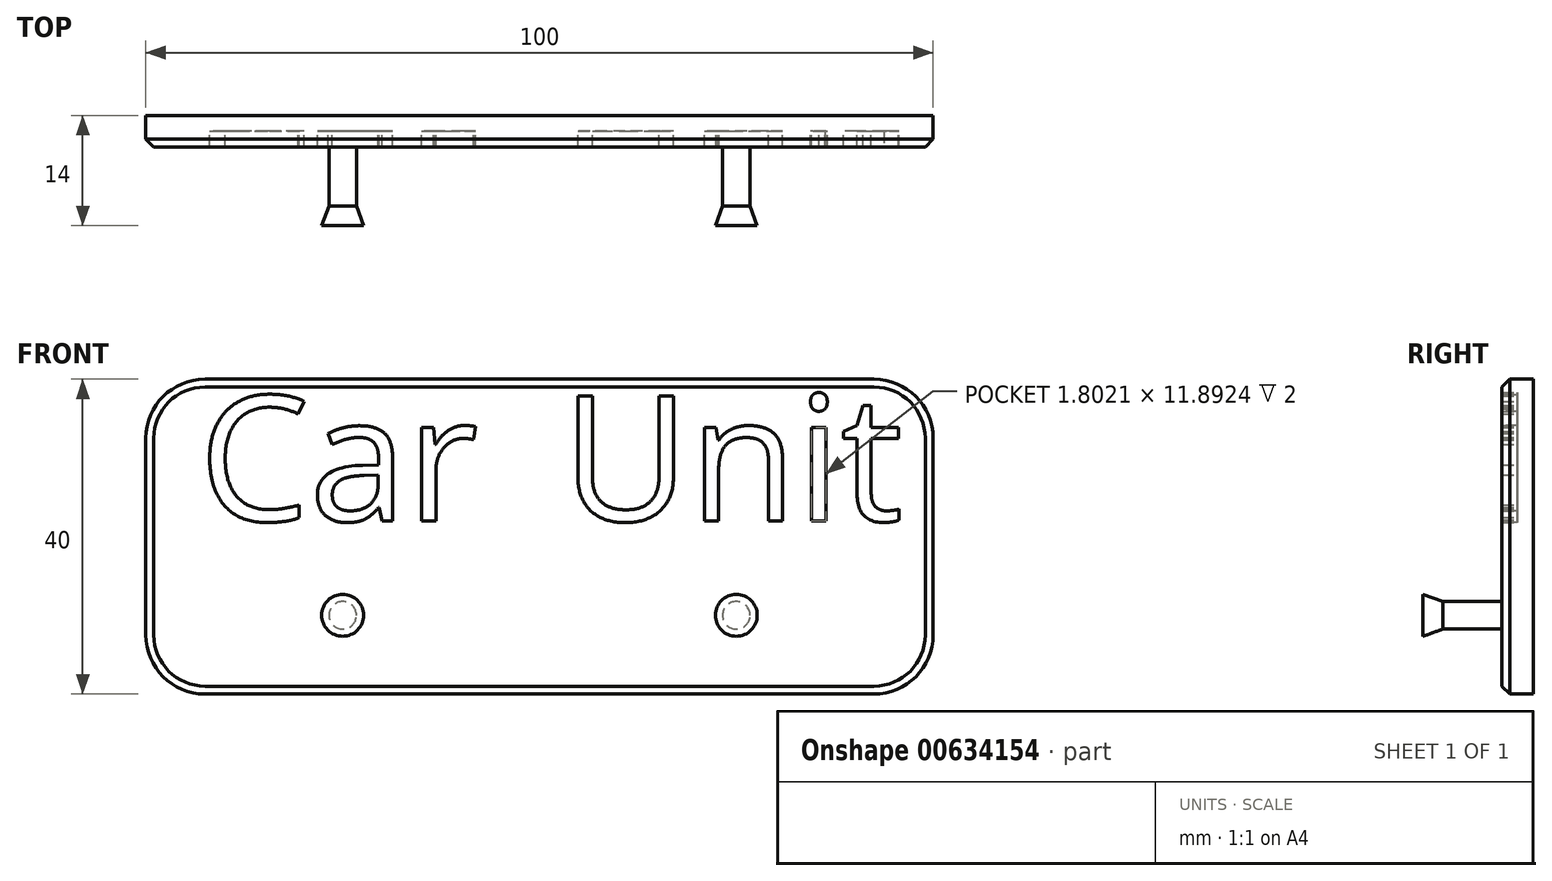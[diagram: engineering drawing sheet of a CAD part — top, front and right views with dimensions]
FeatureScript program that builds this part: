
annotation { "Feature Type Name" : "Feature", "Feature Type Description" : "" }
export const myFeature = defineFeature(function(context is Context, id is Id, definition is map)
    precondition{}
    {
        {
            var Q0;
            Q0=qCreatedBy(makeId("Front.planeOp"),FACE);
            var sketch = newSketch(context, id + "F0", { "sketchPlane" : qUnion([Q0])});
            skLineSegment(sketch, "E0.bottom", {"start": v(-50, 20) * mm, "end": v(50, 20) * mm});
            skLineSegment(sketch, "E0.top", {"start": v(-50, -20) * mm, "end": v(50, -20) * mm});
            skLineSegment(sketch, "E0.left", {"start": v(-50, 20) * mm, "end": v(-50, -20) * mm});
            skLineSegment(sketch, "E0.right", {"start": v(50, 20) * mm, "end": v(50, -20) * mm});
            skText(sketch, "E1", { "text": "Car\n", "fontName": "OpenSans-Regular.ttf"});
            skText(sketch, "E2", { "text": "Unit\n", "fontName": "OpenSans-Regular.ttf"});
            const initialGuessF0  = {"E1": [-0.04325, 0.002, 1, 0, 0.016], "E2": [0.00286, 0.002, 1, 0, 0.016]};
            skSetInitialGuess(sketch, initialGuessF0);
            skSolve(sketch);
        }
        {
            var Q0;
            Q0=makeQuery(id+"F0.imprint","IMPRINT",FACE,{"disambiguationData":[TD([[makeQuery(id+"F0.imprint","IMPRINT",EDGE,{"derivedFrom":sQuery(id+"F0.wireOp",EDGE,"E2.sketch_text.stroke-31")}),-1.0]])]});
            var Q1;
            Q1=makeQuery(id+"F0.imprint","IMPRINT",FACE,{"disambiguationData":[TD([[makeQuery(id+"F0.imprint","IMPRINT",EDGE,{"derivedFrom":sQuery(id+"F0.wireOp",EDGE,"E2.sketch_text.stroke-35")}),-1.0]])]});
            var Q2;
            Q2=makeQuery(id+"F0.imprint","IMPRINT",FACE,{"disambiguationData":[TD([[makeQuery(id+"F0.imprint","IMPRINT",EDGE,{"derivedFrom":sQuery(id+"F0.wireOp",EDGE,"E0.bottom")}),-1.0]])]});
            var Q3;
            Q3=makeQuery(id+"F0.imprint","IMPRINT",FACE,{"disambiguationData":[TD([[makeQuery(id+"F0.imprint","IMPRINT",EDGE,{"derivedFrom":sQuery(id+"F0.wireOp",EDGE,"E2.sketch_text.stroke-43")}),-1.0]])]});
            var Q4;
            Q4=makeQuery(id+"F0.imprint","IMPRINT",FACE,{"disambiguationData":[TD([[makeQuery(id+"F0.imprint","IMPRINT",EDGE,{"derivedFrom":sQuery(id+"F0.wireOp",EDGE,"E2.sketch_text.stroke-14")}),-1.0]])]});
            var Q5;
            Q5=makeQuery(id+"F0.imprint","IMPRINT",FACE,{"disambiguationData":[TD([[makeQuery(id+"F0.imprint","IMPRINT",EDGE,{"derivedFrom":sQuery(id+"F0.wireOp",EDGE,"E2.sketch_text.stroke-0")}),-1.0]])]});
            var Q6;
            Q6=makeQuery(id+"F0.imprint","IMPRINT",FACE,{"disambiguationData":[TD([[makeQuery(id+"F0.imprint","IMPRINT",EDGE,{"derivedFrom":sQuery(id+"F0.wireOp",EDGE,"E1.sketch_text.stroke-42")}),-1.0]])]});
            var Q7;
            Q7=makeQuery(id+"F0.imprint","IMPRINT",FACE,{"disambiguationData":[TD([[makeQuery(id+"F0.imprint","IMPRINT",EDGE,{"derivedFrom":sQuery(id+"F0.wireOp",EDGE,"E1.sketch_text.stroke-34")}),1.0]])]});
            var Q8;
            Q8=makeQuery(id+"F0.imprint","IMPRINT",FACE,{"disambiguationData":[TD([[makeQuery(id+"F0.imprint","IMPRINT",EDGE,{"derivedFrom":sQuery(id+"F0.wireOp",EDGE,"E1.sketch_text.stroke-15")}),-1.0]])]});
            var Q9;
            Q9=makeQuery(id+"F0.imprint","IMPRINT",FACE,{"disambiguationData":[TD([[makeQuery(id+"F0.imprint","IMPRINT",EDGE,{"derivedFrom":sQuery(id+"F0.wireOp",EDGE,"E1.sketch_text.stroke-0")}),-1.0]])]});
            extrude(context, id + "F1", {"entities" : qUnion([Q0, Q1, Q2, Q3, Q4, Q5, Q6, Q7, Q8, Q9]), "oppositeDirection" : true, "depth" : 2 * mm, "offsetDistance" : 25 * mm});
        }
        {
            var Q0;
            Q0=makeQuery(id+"F0.imprint","IMPRINT",FACE,{"disambiguationData":[TD([[makeQuery(id+"F0.imprint","IMPRINT",EDGE,{"derivedFrom":sQuery(id+"F0.wireOp",EDGE,"E0.bottom")}),-1.0]])]});
            var Q1;
            Q1=makeQuery(id+"F0.imprint","IMPRINT",FACE,{"disambiguationData":[TD([[makeQuery(id+"F0.imprint","IMPRINT",EDGE,{"derivedFrom":sQuery(id+"F0.wireOp",EDGE,"E1.sketch_text.stroke-34")}),1.0]])]});
            extrude(context, id + "F2", {"entities" : qUnion([Q0, Q1]), "operationType" : NewBodyOperationType.ADD, "depth" : 2 * mm, "offsetDistance" : 25 * mm});
        }
        {
            var Q0;
            Q0=makeQuery(id+"F2.opExtrude","CAP_FACE",FACE,{"disambiguationData":[OSD([sQuery(id+"F0.wireOp",EDGE,"E0.bottom"),sQuery(id+"F0.wireOp",EDGE,"E0.top"),sQuery(id+"F0.wireOp",EDGE,"E0.left"),sQuery(id+"F0.wireOp",EDGE,"E0.right"),sQuery(id+"F0.wireOp",EDGE,"E1.sketch_text.stroke-0"),sQuery(id+"F0.wireOp",EDGE,"E1.sketch_text.stroke-1"),sQuery(id+"F0.wireOp",EDGE,"E1.sketch_text.stroke-2"),sQuery(id+"F0.wireOp",EDGE,"E1.sketch_text.stroke-3"),sQuery(id+"F0.wireOp",EDGE,"E1.sketch_text.stroke-4"),sQuery(id+"F0.wireOp",EDGE,"E1.sketch_text.stroke-5"),sQuery(id+"F0.wireOp",EDGE,"E1.sketch_text.stroke-6"),sQuery(id+"F0.wireOp",EDGE,"E1.sketch_text.stroke-7"),sQuery(id+"F0.wireOp",EDGE,"E1.sketch_text.stroke-8"),sQuery(id+"F0.wireOp",EDGE,"E1.sketch_text.stroke-9"),sQuery(id+"F0.wireOp",EDGE,"E1.sketch_text.stroke-10"),sQuery(id+"F0.wireOp",EDGE,"E1.sketch_text.stroke-11"),sQuery(id+"F0.wireOp",EDGE,"E1.sketch_text.stroke-12"),sQuery(id+"F0.wireOp",EDGE,"E1.sketch_text.stroke-13"),sQuery(id+"F0.wireOp",EDGE,"E1.sketch_text.stroke-14"),sQuery(id+"F0.wireOp",EDGE,"E1.sketch_text.stroke-15"),sQuery(id+"F0.wireOp",EDGE,"E1.sketch_text.stroke-16"),sQuery(id+"F0.wireOp",EDGE,"E1.sketch_text.stroke-17"),sQuery(id+"F0.wireOp",EDGE,"E1.sketch_text.stroke-18"),sQuery(id+"F0.wireOp",EDGE,"E1.sketch_text.stroke-19"),sQuery(id+"F0.wireOp",EDGE,"E1.sketch_text.stroke-20"),sQuery(id+"F0.wireOp",EDGE,"E1.sketch_text.stroke-21"),sQuery(id+"F0.wireOp",EDGE,"E1.sketch_text.stroke-22"),sQuery(id+"F0.wireOp",EDGE,"E1.sketch_text.stroke-23"),sQuery(id+"F0.wireOp",EDGE,"E1.sketch_text.stroke-24"),sQuery(id+"F0.wireOp",EDGE,"E1.sketch_text.stroke-25"),sQuery(id+"F0.wireOp",EDGE,"E1.sketch_text.stroke-26"),sQuery(id+"F0.wireOp",EDGE,"E1.sketch_text.stroke-27"),sQuery(id+"F0.wireOp",EDGE,"E1.sketch_text.stroke-28"),sQuery(id+"F0.wireOp",EDGE,"E1.sketch_text.stroke-29"),sQuery(id+"F0.wireOp",EDGE,"E1.sketch_text.stroke-30"),sQuery(id+"F0.wireOp",EDGE,"E1.sketch_text.stroke-31"),sQuery(id+"F0.wireOp",EDGE,"E1.sketch_text.stroke-32"),sQuery(id+"F0.wireOp",EDGE,"E1.sketch_text.stroke-33"),sQuery(id+"F0.wireOp",EDGE,"E1.sketch_text.stroke-42"),sQuery(id+"F0.wireOp",EDGE,"E1.sketch_text.stroke-43"),sQuery(id+"F0.wireOp",EDGE,"E1.sketch_text.stroke-44"),sQuery(id+"F0.wireOp",EDGE,"E1.sketch_text.stroke-45"),sQuery(id+"F0.wireOp",EDGE,"E1.sketch_text.stroke-46"),sQuery(id+"F0.wireOp",EDGE,"E1.sketch_text.stroke-47"),sQuery(id+"F0.wireOp",EDGE,"E1.sketch_text.stroke-48"),sQuery(id+"F0.wireOp",EDGE,"E1.sketch_text.stroke-49"),sQuery(id+"F0.wireOp",EDGE,"E1.sketch_text.stroke-50"),sQuery(id+"F0.wireOp",EDGE,"E1.sketch_text.stroke-51"),sQuery(id+"F0.wireOp",EDGE,"E1.sketch_text.stroke-52"),sQuery(id+"F0.wireOp",EDGE,"E1.sketch_text.stroke-53"),sQuery(id+"F0.wireOp",EDGE,"E1.sketch_text.stroke-54"),sQuery(id+"F0.wireOp",EDGE,"E2.sketch_text.stroke-0"),sQuery(id+"F0.wireOp",EDGE,"E2.sketch_text.stroke-1"),sQuery(id+"F0.wireOp",EDGE,"E2.sketch_text.stroke-2"),sQuery(id+"F0.wireOp",EDGE,"E2.sketch_text.stroke-3"),sQuery(id+"F0.wireOp",EDGE,"E2.sketch_text.stroke-4"),sQuery(id+"F0.wireOp",EDGE,"E2.sketch_text.stroke-5"),sQuery(id+"F0.wireOp",EDGE,"E2.sketch_text.stroke-6"),sQuery(id+"F0.wireOp",EDGE,"E2.sketch_text.stroke-7"),sQuery(id+"F0.wireOp",EDGE,"E2.sketch_text.stroke-8"),sQuery(id+"F0.wireOp",EDGE,"E2.sketch_text.stroke-9"),sQuery(id+"F0.wireOp",EDGE,"E2.sketch_text.stroke-10"),sQuery(id+"F0.wireOp",EDGE,"E2.sketch_text.stroke-11"),sQuery(id+"F0.wireOp",EDGE,"E2.sketch_text.stroke-12"),sQuery(id+"F0.wireOp",EDGE,"E2.sketch_text.stroke-13"),sQuery(id+"F0.wireOp",EDGE,"E2.sketch_text.stroke-14"),sQuery(id+"F0.wireOp",EDGE,"E2.sketch_text.stroke-15"),sQuery(id+"F0.wireOp",EDGE,"E2.sketch_text.stroke-16"),sQuery(id+"F0.wireOp",EDGE,"E2.sketch_text.stroke-17"),sQuery(id+"F0.wireOp",EDGE,"E2.sketch_text.stroke-18"),sQuery(id+"F0.wireOp",EDGE,"E2.sketch_text.stroke-19"),sQuery(id+"F0.wireOp",EDGE,"E2.sketch_text.stroke-20"),sQuery(id+"F0.wireOp",EDGE,"E2.sketch_text.stroke-21"),sQuery(id+"F0.wireOp",EDGE,"E2.sketch_text.stroke-22"),sQuery(id+"F0.wireOp",EDGE,"E2.sketch_text.stroke-23"),sQuery(id+"F0.wireOp",EDGE,"E2.sketch_text.stroke-24"),sQuery(id+"F0.wireOp",EDGE,"E2.sketch_text.stroke-25"),sQuery(id+"F0.wireOp",EDGE,"E2.sketch_text.stroke-26"),sQuery(id+"F0.wireOp",EDGE,"E2.sketch_text.stroke-27"),sQuery(id+"F0.wireOp",EDGE,"E2.sketch_text.stroke-28"),sQuery(id+"F0.wireOp",EDGE,"E2.sketch_text.stroke-29"),sQuery(id+"F0.wireOp",EDGE,"E2.sketch_text.stroke-30"),sQuery(id+"F0.wireOp",EDGE,"E2.sketch_text.stroke-31"),sQuery(id+"F0.wireOp",EDGE,"E2.sketch_text.stroke-32"),sQuery(id+"F0.wireOp",EDGE,"E2.sketch_text.stroke-33"),sQuery(id+"F0.wireOp",EDGE,"E2.sketch_text.stroke-34"),sQuery(id+"F0.wireOp",EDGE,"E2.sketch_text.stroke-35"),sQuery(id+"F0.wireOp",EDGE,"E2.sketch_text.stroke-36"),sQuery(id+"F0.wireOp",EDGE,"E2.sketch_text.stroke-37"),sQuery(id+"F0.wireOp",EDGE,"E2.sketch_text.stroke-38"),sQuery(id+"F0.wireOp",EDGE,"E2.sketch_text.stroke-39"),sQuery(id+"F0.wireOp",EDGE,"E2.sketch_text.stroke-40"),sQuery(id+"F0.wireOp",EDGE,"E2.sketch_text.stroke-41"),sQuery(id+"F0.wireOp",EDGE,"E2.sketch_text.stroke-42"),sQuery(id+"F0.wireOp",EDGE,"E2.sketch_text.stroke-43"),sQuery(id+"F0.wireOp",EDGE,"E2.sketch_text.stroke-44"),sQuery(id+"F0.wireOp",EDGE,"E2.sketch_text.stroke-45"),sQuery(id+"F0.wireOp",EDGE,"E2.sketch_text.stroke-46"),sQuery(id+"F0.wireOp",EDGE,"E2.sketch_text.stroke-47"),sQuery(id+"F0.wireOp",EDGE,"E2.sketch_text.stroke-48"),sQuery(id+"F0.wireOp",EDGE,"E2.sketch_text.stroke-49"),sQuery(id+"F0.wireOp",EDGE,"E2.sketch_text.stroke-50"),sQuery(id+"F0.wireOp",EDGE,"E2.sketch_text.stroke-51"),sQuery(id+"F0.wireOp",EDGE,"E2.sketch_text.stroke-52"),sQuery(id+"F0.wireOp",EDGE,"E2.sketch_text.stroke-53"),sQuery(id+"F0.wireOp",EDGE,"E2.sketch_text.stroke-54"),sQuery(id+"F0.wireOp",EDGE,"E2.sketch_text.stroke-55"),sQuery(id+"F0.wireOp",EDGE,"E2.sketch_text.stroke-56"),sQuery(id+"F0.wireOp",EDGE,"E2.sketch_text.stroke-57"),sQuery(id+"F0.wireOp",EDGE,"E2.sketch_text.stroke-58"),sQuery(id+"F0.wireOp",EDGE,"E2.sketch_text.stroke-59"),sQuery(id+"F0.wireOp",EDGE,"E2.sketch_text.stroke-60"),sQuery(id+"F0.wireOp",EDGE,"E2.sketch_text.stroke-61")])],"isStart":false});
            var sketch = newSketch(context, id + "F3", { "sketchPlane" : qUnion([Q0])});
            skCircle(sketch, "E3", {"center": v(-25, -10) * mm, "radius": 1.75 * mm});
            skLineSegment(sketch, "E4", {"start": v(0, 0) * mm, "end": v(0, -13.03) * mm, "construction": true});
            skCircle(sketch, "E5.MirrorC", {"center": v(25, -10) * mm, "radius": 1.75 * mm});
            skSolve(sketch);
        }
        {
            var Q0;
            Q0 = qSketchRegion(id + "F3", true);
            extrude(context, id + "F4", {"entities" : qUnion([Q0]), "operationType" : NewBodyOperationType.ADD, "depth" : 7.5 * mm, "offsetDistance" : 25 * mm});
        }
        {
            var Q0;
            Q0=makeQuery(id+"F4.opExtrude","CAP_FACE",FACE,{"disambiguationData":[OSD([sQuery(id+"F3.wireOp",EDGE,"E3")])],"isStart":false});
            var Q1;
            Q1=makeQuery(id+"F4.opExtrude","CAP_FACE",FACE,{"disambiguationData":[OSD([sQuery(id+"F3.wireOp",EDGE,"E5.MirrorC")])],"isStart":false});
            extrude(context, id + "F5", {"entities" : qUnion([Q0, Q1]), "operationType" : NewBodyOperationType.ADD, "depth" : 2.5 * mm, "offsetDistance" : 25 * mm, "hasDraft" : true, "draftAngle" : 20 * degree});
        }
        {
            var Q0;
            {var subQ0=sQuery(id+"F0.wireOp",EDGE,"E0.left");var subQ1=sQuery(id+"F0.wireOp",EDGE,"E0.bottom");Q0=makeQuery(id+"F2.boolean.opBoolean","MERGE",EDGE,{"derivedFrom":[makeQuery(id+"F1.opExtrude","SWEPT_EDGE",EDGE,{"disambiguationData":[OSD([subQ1,subQ0])]}),makeQuery(id+"F2.opExtrude","SWEPT_EDGE",EDGE,{"disambiguationData":[OSD([subQ1,subQ0])]})]});}
            var Q1;
            {var subQ0=sQuery(id+"F0.wireOp",EDGE,"E0.right");var subQ1=sQuery(id+"F0.wireOp",EDGE,"E0.bottom");Q1=makeQuery(id+"F2.boolean.opBoolean","MERGE",EDGE,{"derivedFrom":[makeQuery(id+"F1.opExtrude","SWEPT_EDGE",EDGE,{"disambiguationData":[OSD([subQ1,subQ0])]}),makeQuery(id+"F2.opExtrude","SWEPT_EDGE",EDGE,{"disambiguationData":[OSD([subQ1,subQ0])]})]});}
            var Q2;
            {var subQ0=sQuery(id+"F0.wireOp",EDGE,"E0.right");var subQ1=sQuery(id+"F0.wireOp",EDGE,"E0.top");Q2=makeQuery(id+"F2.boolean.opBoolean","MERGE",EDGE,{"derivedFrom":[makeQuery(id+"F1.opExtrude","SWEPT_EDGE",EDGE,{"disambiguationData":[OSD([subQ1,subQ0])]}),makeQuery(id+"F2.opExtrude","SWEPT_EDGE",EDGE,{"disambiguationData":[OSD([subQ1,subQ0])]})]});}
            var Q3;
            {var subQ0=sQuery(id+"F0.wireOp",EDGE,"E0.left");var subQ1=sQuery(id+"F0.wireOp",EDGE,"E0.top");Q3=makeQuery(id+"F2.boolean.opBoolean","MERGE",EDGE,{"derivedFrom":[makeQuery(id+"F1.opExtrude","SWEPT_EDGE",EDGE,{"disambiguationData":[OSD([subQ1,subQ0])]}),makeQuery(id+"F2.opExtrude","SWEPT_EDGE",EDGE,{"disambiguationData":[OSD([subQ1,subQ0])]})]});}
            fillet(context, id + "F6", {"entities" : qUnion([Q0, Q1, Q2, Q3]), "radius" : 7.5 * mm, "tangentPropagation" : true, "allowEdgeOverflow" : false});
        }
        {
            var Q0;
            Q0=makeQuery(id+"F2.opExtrude","CAP_EDGE",EDGE,{"disambiguationData":[OSD([sQuery(id+"F0.wireOp",EDGE,"E0.left")])],"isStart":false});
            var Q1;
            Q1=makeQuery(id+"F4.opExtrude","CAP_EDGE",EDGE,{"disambiguationData":[OSD([sQuery(id+"F3.wireOp",EDGE,"E3")])],"isStart":true});
            var Q2;
            Q2=makeQuery(id+"F4.opExtrude","CAP_EDGE",EDGE,{"disambiguationData":[OSD([sQuery(id+"F3.wireOp",EDGE,"E5.MirrorC")])],"isStart":true});
            chamfer(context, id + "F7", {"entities" : qUnion([Q0, Q1, Q2]), "width" : 1 * mm, "tangentPropagation" : true});
        }
    });
